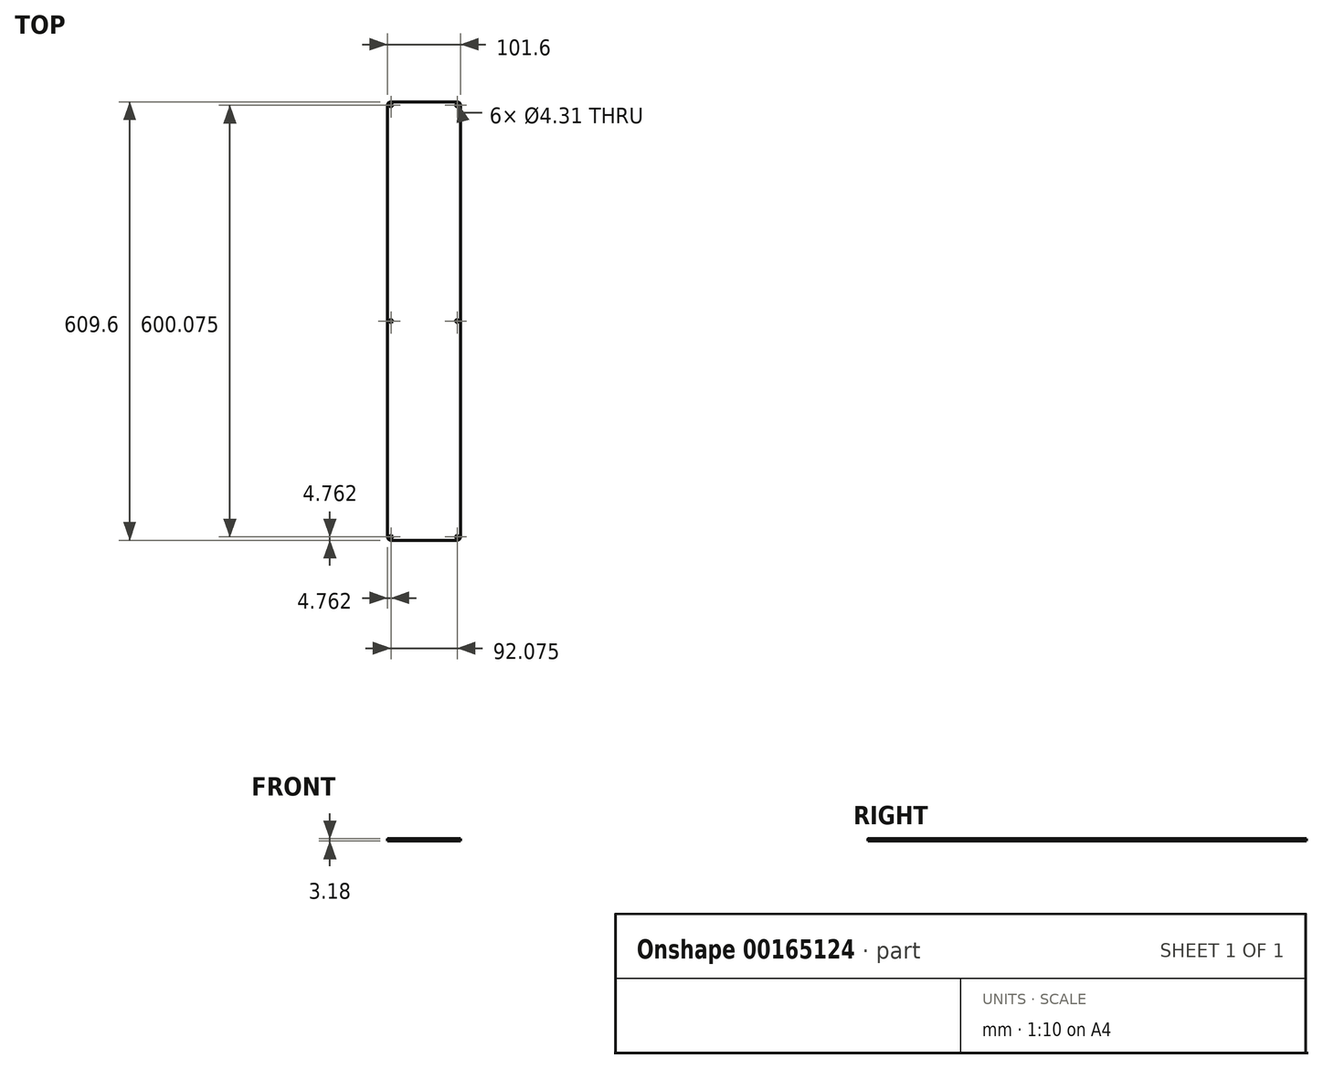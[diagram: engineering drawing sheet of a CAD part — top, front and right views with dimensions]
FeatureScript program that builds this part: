
annotation { "Feature Type Name" : "Feature", "Feature Type Description" : "" }
export const myFeature = defineFeature(function(context is Context, id is Id, definition is map)
    precondition{}
    {
        {
            var Q0;
            Q0=qCreatedBy(makeId("Top.planeOp"),FACE);
            var sketch = newSketch(context, id + "F0", { "sketchPlane" : qUnion([Q0])});
            skLineSegment(sketch, "E0.bottom", {"start": v(-50.8, 304.8) * mm, "end": v(50.8, 304.8) * mm});
            skLineSegment(sketch, "E0.top", {"start": v(-50.8, -304.8) * mm, "end": v(50.8, -304.8) * mm});
            skLineSegment(sketch, "E0.left", {"start": v(-50.8, 304.8) * mm, "end": v(-50.8, -304.8) * mm});
            skLineSegment(sketch, "E0.right", {"start": v(50.8, 304.8) * mm, "end": v(50.8, -304.8) * mm});
            skPoint(sketch, "E0.middle", {"position": v(0, 0) * mm});
            skLineSegment(sketch, "E1.bottom", {"start": v(-46.04, 300.04) * mm, "end": v(46.04, 300.04) * mm, "construction": true});
            skLineSegment(sketch, "E1.top", {"start": v(-46.04, -300.04) * mm, "end": v(46.04, -300.04) * mm, "construction": true});
            skLineSegment(sketch, "E1.left", {"start": v(-46.04, 300.04) * mm, "end": v(-46.04, -300.04) * mm, "construction": true});
            skLineSegment(sketch, "E1.right", {"start": v(46.04, 300.04) * mm, "end": v(46.04, -300.04) * mm, "construction": true});
            skLineSegment(sketch, "E2", {"start": v(0, 300.04) * mm, "end": v(0, 304.8) * mm, "construction": true});
            skLineSegment(sketch, "E3", {"start": v(-46.04, 0) * mm, "end": v(-50.8, 0) * mm, "construction": true});
            skCircle(sketch, "E4", {"center": v(-46.04, 300.04) * mm, "radius": 2.15 * mm});
            skCircle(sketch, "E5", {"center": v(-46.04, 0) * mm, "radius": 2.15 * mm});
            skCircle(sketch, "E6", {"center": v(-46.04, -300.04) * mm, "radius": 2.15 * mm});
            skCircle(sketch, "E7", {"center": v(46.04, -300.04) * mm, "radius": 2.15 * mm});
            skCircle(sketch, "E8", {"center": v(46.04, 0) * mm, "radius": 2.15 * mm});
            skCircle(sketch, "E9", {"center": v(46.04, 300.04) * mm, "radius": 2.15 * mm});
            skSolve(sketch);
        }
        {
            var Q0;
            Q0 = qSketchRegion(id + "F0", true);
            extrude(context, id + "F1", {"entities" : qUnion([Q0]), "depth" : 3.17 * mm});
        }
        {
            var Q0;
            Q0=makeQuery(id+"F1.opExtrude","SWEPT_EDGE",EDGE,{"disambiguationData":[OSD([sQuery(id+"F0.wireOp",EDGE,"E0.bottom"),sQuery(id+"F0.wireOp",EDGE,"E0.left")])]});
            var Q1;
            Q1=makeQuery(id+"F1.opExtrude","SWEPT_EDGE",EDGE,{"disambiguationData":[OSD([sQuery(id+"F0.wireOp",EDGE,"E0.bottom"),sQuery(id+"F0.wireOp",EDGE,"E0.right")])]});
            var Q2;
            Q2=makeQuery(id+"F1.opExtrude","SWEPT_EDGE",EDGE,{"disambiguationData":[OSD([sQuery(id+"F0.wireOp",EDGE,"E0.top"),sQuery(id+"F0.wireOp",EDGE,"E0.right")])]});
            var Q3;
            Q3=makeQuery(id+"F1.opExtrude","SWEPT_EDGE",EDGE,{"disambiguationData":[OSD([sQuery(id+"F0.wireOp",EDGE,"E0.top"),sQuery(id+"F0.wireOp",EDGE,"E0.left")])]});
            fillet(context, id + "F2", {"entities" : qUnion([Q0, Q1, Q2, Q3]), "radius" : 4.76 * mm, "tangentPropagation" : true, "allowEdgeOverflow" : false});
        }
    });
